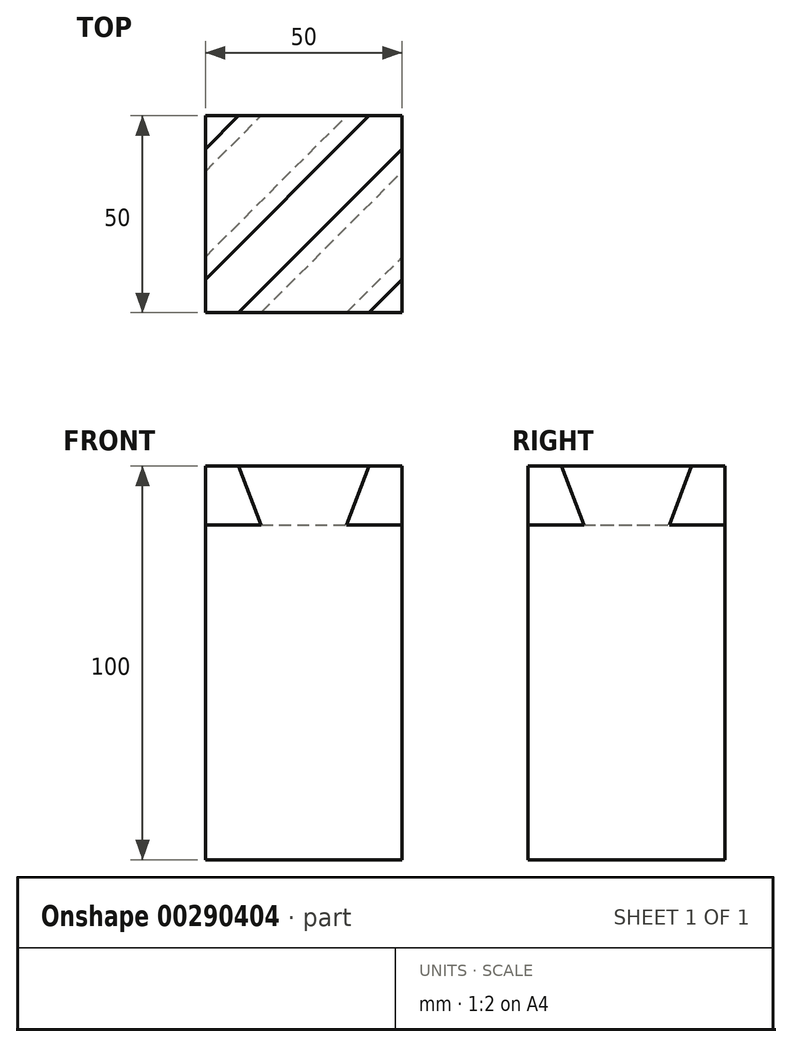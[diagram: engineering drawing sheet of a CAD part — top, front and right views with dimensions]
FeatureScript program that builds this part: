
annotation { "Feature Type Name" : "Feature", "Feature Type Description" : "" }
export const myFeature = defineFeature(function(context is Context, id is Id, definition is map)
    precondition{}
    {
        {
            var Q0;
            Q0=qCreatedBy(makeId("Top.planeOp"),FACE);
            var sketch = newSketch(context, id + "F0", { "sketchPlane" : qUnion([Q0])});
            skLineSegment(sketch, "E0.bottom", {"start": v(25, 25) * mm, "end": v(-25, 25) * mm});
            skLineSegment(sketch, "E0.top", {"start": v(25, -25) * mm, "end": v(-25, -25) * mm});
            skLineSegment(sketch, "E0.left", {"start": v(25, 25) * mm, "end": v(25, -25) * mm});
            skLineSegment(sketch, "E0.right", {"start": v(-25, 25) * mm, "end": v(-25, -25) * mm});
            skPoint(sketch, "E0.middle", {"position": v(0, 0) * mm});
            skSolve(sketch);
        }
        {
            var Q0;
            Q0 = qSketchRegion(id + "F0", true);
            extrude(context, id + "F1", {"entities" : qUnion([Q0]), "depth" : 100 * mm});
        }
        {
            var Q0;
            Q0=makeQuery(id+"F1.opExtrude","CAP_VERTEX",VERTEX,{"disambiguationData":[OSD([sQuery(id+"F0.wireOp",EDGE,"E0.top"),sQuery(id+"F0.wireOp",EDGE,"E0.left")])],"isStart":false});
            var Q1;
            Q1=makeQuery(id+"F1.opExtrude","CAP_VERTEX",VERTEX,{"disambiguationData":[OSD([sQuery(id+"F0.wireOp",EDGE,"E0.bottom"),sQuery(id+"F0.wireOp",EDGE,"E0.right")])],"isStart":false});
            var Q2;
            Q2=makeQuery(id+"F1.opExtrude","CAP_VERTEX",VERTEX,{"disambiguationData":[OSD([sQuery(id+"F0.wireOp",EDGE,"E0.top"),sQuery(id+"F0.wireOp",EDGE,"E0.left")])],"isStart":true});
            cPlane(context, id + "F2", {"entities" : qUnion([Q0, Q1, Q2]), "cplaneType" : CPlaneType.THREE_POINT, "offset" : 25 * mm, "width" : 150 * mm, "height" : 150 * mm});
        }
        {
            var Q0;
            Q0=qCreatedBy(id+"F2.planeOp",FACE);
            var sketch = newSketch(context, id + "F3", { "sketchPlane" : qUnion([Q0])});
            skLineSegment(sketch, "E1", {"start": v(0, 0) * mm, "end": v(0, 131.14) * mm, "construction": true});
            skLineSegment(sketch, "E2", {"start": v(5.98, 100) * mm, "end": v(10, 85) * mm});
            skLineSegment(sketch, "E3", {"start": v(10, 85) * mm, "end": v(-10, 85) * mm});
            skLineSegment(sketch, "E4", {"start": v(-10, 85) * mm, "end": v(-5.98, 100) * mm});
            skLineSegment(sketch, "E5", {"start": v(-5.98, 100) * mm, "end": v(5.98, 100) * mm});
            skLineSegment(sketch, "E6", {"start": v(41.34, 100) * mm, "end": v(29.37, 100) * mm});
            skLineSegment(sketch, "E7", {"start": v(29.37, 100) * mm, "end": v(25.36, 85) * mm});
            skLineSegment(sketch, "E8", {"start": v(25.36, 85) * mm, "end": v(45.36, 85) * mm});
            skLineSegment(sketch, "E9", {"start": v(45.36, 85) * mm, "end": v(41.34, 100) * mm});
            skLineSegment(sketch, "E10", {"start": v(35.36, 100) * mm, "end": v(35.36, 85) * mm, "construction": true});
            skLineSegment(sketch, "E11", {"start": v(-29.37, 100) * mm, "end": v(-25.36, 85) * mm});
            skLineSegment(sketch, "E12", {"start": v(-25.36, 85) * mm, "end": v(-45.36, 85) * mm});
            skLineSegment(sketch, "E13", {"start": v(-45.36, 85) * mm, "end": v(-41.34, 100) * mm});
            skLineSegment(sketch, "E14", {"start": v(-41.34, 100) * mm, "end": v(-29.37, 100) * mm});
            skLineSegment(sketch, "E15", {"start": v(-35.36, 100) * mm, "end": v(-35.36, 85) * mm, "construction": true});
            skSolve(sketch);
        }
        {
            var Q0;
            Q0 = qSketchRegion(id + "F3", true);
            extrude(context, id + "F4", {"entities" : qUnion([Q0]), "operationType" : NewBodyOperationType.REMOVE, "endBound" : BoundingType.SYMMETRIC, "oppositeDirection" : true, "depth" : 100 * mm});
        }
    });
